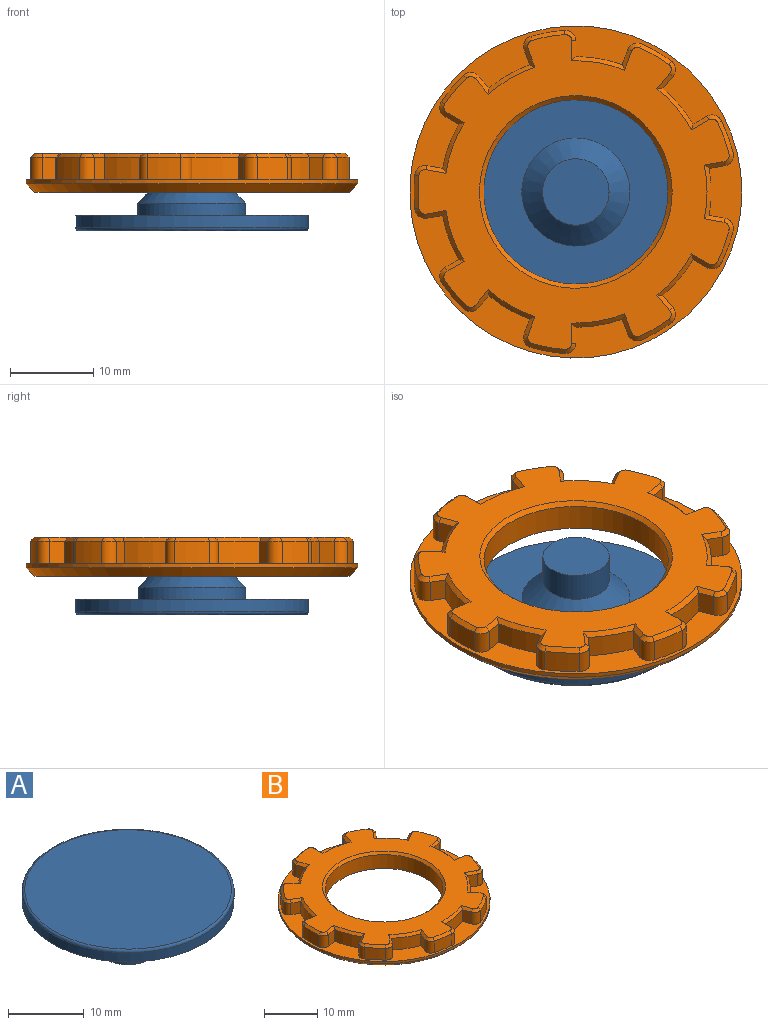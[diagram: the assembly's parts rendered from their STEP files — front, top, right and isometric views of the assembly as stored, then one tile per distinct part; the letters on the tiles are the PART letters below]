
ASSEMBLY  parts=2 mates=1
PART A: 8 faces, bbox 30.3x30.3x9.4 mm
  f0: plane 27.3x27.3mm, normal (0,0,1), area 585.3mm2, adj f7
  f1: plane 8x8mm, normal (0,0,-1), area 50.3mm2, adj f2
  f2: cylinder r=4mm len=8mm, axis (0,0,1), area 88mm2, adj f1,f3
  f3: cone r=4mm half-angle=45deg, axis (0,0,1), area 116.6mm2, adj f2,f4
  f4: cylinder r=6.5mm len=13mm, axis (0,0,1), area 61.3mm2, adj f3,f5
  f5: plane 28x28mm, normal (0,0,-1), area 483mm2, adj f4,f6
  f6: cylinder r=14mm len=28mm, axis (0,0,1), area 131.9mm2, adj f5,f7
  f7: torus R=13.65mm, axis (0,0,1), area 47.9mm2, adj f0,f6
PART B: 117 faces, bbox 40x40x4.7 mm
  f0: cylinder r=11.1mm len=22.2mm, axis (0,0,-1), area 223.2mm2, adj f110,f115
  f1: cylinder r=16.3mm len=5.32mm, axis (0,0,-1), area 15.4mm2, adj f2,f53,f97,f113
  f2: plane 2.7x1.88mm, normal (0.17,0.98,0), area 5.1mm2, adj f1,f7,f95,f113
  f3: cylinder r=19.5mm len=4.13mm, axis (0,0,-1), area 11.2mm2, adj f7,f8,f91,f113
  f4: plane 2.7x1.88mm, normal (0.17,-0.98,0), area 5.1mm2, adj f5,f8,f87,f113
  f5: cylinder r=16.3mm len=5.32mm, axis (0,0,-1), area 15.4mm2, adj f4,f9,f85,f113
  f6: plane 37.91x37.46mm, normal (0,0,1), area 505.2mm2, adj f56,f57,f58,f59,f60,f61,f62,f63
  f7: cylinder r=1.25mm len=2.7mm, axis (0,0,-1), area 5.5mm2, adj f2,f3,f93,f113
  f8: cylinder r=1.25mm len=2.7mm, axis (0,0,-1), area 5.5mm2, adj f3,f4,f89,f113
  f9: plane 2.7x1.65mm, normal (-0.5,0.87,0), area 5.1mm2, adj f5,f13,f83,f113
  f10: cylinder r=19.5mm len=3.16mm, axis (0,0,-1), area 11.2mm2, adj f13,f14,f79,f113
  f11: plane 2.7x1.46mm, normal (0.77,-0.64,0), area 5.1mm2, adj f12,f14,f75,f113
  f12: cylinder r=16.3mm len=4.9mm, axis (0,0,-1), area 15.4mm2, adj f11,f15,f73,f113
  f13: cylinder r=1.25mm len=2.7mm, axis (0,0,-1), area 5.5mm2, adj f9,f10,f81,f113
  f14: cylinder r=1.25mm len=2.7mm, axis (0,0,-1), area 5.5mm2, adj f10,f11,f77,f113
  f15: plane 2.7x1.79mm, normal (-0.94,0.34,0), area 5.1mm2, adj f12,f19,f71,f113
  f16: cylinder r=19.5mm len=4.06mm, axis (0,0,-1), area 11.2mm2, adj f19,f20,f67,f113
  f17: plane 2.7x1.91mm, normal (1,0,0), area 5.1mm2, adj f18,f20,f63,f113
  f18: cylinder r=16.3mm len=5.58mm, axis (0,0,-1), area 15.4mm2, adj f17,f21,f61,f113
  f19: cylinder r=1.25mm len=2.7mm, axis (0,0,-1), area 5.5mm2, adj f15,f16,f69,f113
  f20: cylinder r=1.25mm len=2.7mm, axis (0,0,-1), area 5.5mm2, adj f16,f17,f65,f113
  f21: plane 2.7x1.79mm, normal (-0.94,-0.34,0), area 5.1mm2, adj f18,f25,f59,f113
  f22: cylinder r=19.5mm len=3.57mm, axis (0,0,-1), area 11.2mm2, adj f25,f26,f56,f113
  f23: plane 2.7x1.46mm, normal (0.77,0.64,0), area 5.1mm2, adj f24,f26,f60,f113
  f24: cylinder r=16.3mm len=4.34mm, axis (0,0,-1), area 15.4mm2, adj f23,f27,f62,f113
  f25: cylinder r=1.25mm len=2.7mm, axis (0,0,-1), area 5.5mm2, adj f21,f22,f57,f113
  f26: cylinder r=1.25mm len=2.7mm, axis (0,0,-1), area 5.5mm2, adj f22,f23,f58,f113
  f27: plane 2.7x1.65mm, normal (-0.5,-0.87,0), area 5.1mm2, adj f24,f31,f64,f113
  f28: cylinder r=19.5mm len=3.88mm, axis (0,0,-1), area 11.2mm2, adj f31,f32,f68,f113
  f29: plane 2.7x1.88mm, normal (0.17,0.98,0), area 5.1mm2, adj f30,f32,f72,f113
  f30: cylinder r=16.3mm len=5.66mm, axis (0,0,-1), area 15.4mm2, adj f29,f33,f74,f113
  f31: cylinder r=1.25mm len=2.7mm, axis (0,0,-1), area 5.5mm2, adj f27,f28,f66,f113
  f32: cylinder r=1.25mm len=2.7mm, axis (0,0,-1), area 5.5mm2, adj f28,f29,f70,f113
  f33: plane 2.7x1.88mm, normal (0.17,-0.98,0), area 5.1mm2, adj f30,f37,f76,f113
  f34: cylinder r=19.5mm len=3.88mm, axis (0,0,-1), area 11.2mm2, adj f37,f38,f80,f113
  f35: plane 2.7x1.65mm, normal (-0.5,0.87,0), area 5.1mm2, adj f36,f38,f84,f113
  f36: cylinder r=16.3mm len=4.34mm, axis (0,0,-1), area 15.4mm2, adj f35,f39,f86,f113
  f37: cylinder r=1.25mm len=2.7mm, axis (0,0,-1), area 5.5mm2, adj f33,f34,f78,f113
  f38: cylinder r=1.25mm len=2.7mm, axis (0,0,-1), area 5.5mm2, adj f34,f35,f82,f113
  f39: plane 2.7x1.46mm, normal (0.77,-0.64,0), area 5.1mm2, adj f36,f43,f88,f113
  f40: cylinder r=19.5mm len=3.57mm, axis (0,0,-1), area 11.2mm2, adj f43,f44,f92,f113
  f41: plane 2.7x1.79mm, normal (-0.94,0.34,0), area 5.1mm2, adj f42,f44,f96,f113
  f42: cylinder r=16.3mm len=5.58mm, axis (0,0,-1), area 15.4mm2, adj f41,f45,f98,f113
  f43: cylinder r=1.25mm len=2.7mm, axis (0,0,-1), area 5.5mm2, adj f39,f40,f90,f113
  f44: cylinder r=1.25mm len=2.7mm, axis (0,0,-1), area 5.5mm2, adj f40,f41,f94,f113
  f45: plane 2.7x1.91mm, normal (1,0,0), area 5.1mm2, adj f42,f49,f100,f113
  f46: cylinder r=19.5mm len=4.06mm, axis (0,0,-1), area 11.2mm2, adj f49,f50,f104,f113
  f47: plane 2.7x1.79mm, normal (-0.94,-0.34,0), area 5.1mm2, adj f48,f50,f108,f113
  f48: cylinder r=16.3mm len=4.9mm, axis (0,0,-1), area 15.4mm2, adj f47,f51,f109,f113
  f49: cylinder r=1.25mm len=2.7mm, axis (0,0,-1), area 5.5mm2, adj f45,f46,f102,f113
  f50: cylinder r=1.25mm len=2.7mm, axis (0,0,-1), area 5.5mm2, adj f46,f47,f106,f113
  f51: plane 2.7x1.46mm, normal (0.77,0.64,0), area 5.1mm2, adj f48,f54,f107,f113
  f52: cylinder r=19.5mm len=3.16mm, axis (0,0,-1), area 11.2mm2, adj f54,f55,f103,f113
  f53: plane 2.7x1.65mm, normal (-0.5,-0.87,0), area 5.1mm2, adj f1,f55,f99,f113
  f54: cylinder r=1.25mm len=2.7mm, axis (0,0,-1), area 5.5mm2, adj f51,f52,f105,f113
  f55: cylinder r=1.25mm len=2.7mm, axis (0,0,-1), area 5.5mm2, adj f52,f53,f101,f113
  f56: cone r=19.5mm half-angle=45deg, axis (0,0,-1), area 2.9mm2, adj f6,f22,f57,f58
  f57: cone r=0.75mm half-angle=45deg, axis (0,0,-1), area 1.2mm2, adj f6,f25,f56,f59
  f58: cone r=0.75mm half-angle=45deg, axis (0,0,-1), area 1.2mm2, adj f6,f26,f56,f60
  f59: plane 2.45x1.13mm, normal (-0.66,-0.24,0.71), area 1.5mm2, adj f6,f21,f57,f61
  f60: plane 1.94x1.86mm, normal (0.54,0.45,0.71), area 1.5mm2, adj f6,f23,f58,f62
  f61: cone r=16.3mm half-angle=45deg, axis (0,0,-1), area 4.3mm2, adj f6,f18,f59,f63
  f62: cone r=16.3mm half-angle=45deg, axis (0,0,-1), area 4.3mm2, adj f6,f24,f60,f64
  f63: plane 2.42x0.51mm, normal (0.71,0,0.71), area 1.5mm2, adj f6,f17,f61,f65
  f64: plane 2.1x1.65mm, normal (-0.35,-0.61,0.71), area 1.5mm2, adj f6,f27,f62,f66
  f65: cone r=0.75mm half-angle=45deg, axis (0,0,-1), area 1.2mm2, adj f6,f20,f63,f67
  f66: cone r=0.75mm half-angle=45deg, axis (0,0,-1), area 1.2mm2, adj f6,f31,f64,f68
  f67: cone r=19.5mm half-angle=45deg, axis (0,0,-1), area 2.9mm2, adj f6,f16,f65,f69
  f68: cone r=19.5mm half-angle=45deg, axis (0,0,-1), area 2.9mm2, adj f6,f28,f66,f70
  f69: cone r=0.75mm half-angle=45deg, axis (0,0,-1), area 1.2mm2, adj f6,f19,f67,f71
  f70: cone r=0.75mm half-angle=45deg, axis (0,0,-1), area 1.2mm2, adj f6,f32,f68,f72
  f71: plane 2.28x1.3mm, normal (-0.66,0.24,0.71), area 1.5mm2, adj f6,f15,f69,f73
  f72: plane 2.47x0.83mm, normal (0.12,0.7,0.71), area 1.5mm2, adj f6,f29,f70,f74
  f73: cone r=16.3mm half-angle=45deg, axis (0,0,-1), area 4.3mm2, adj f6,f12,f71,f75
  f74: cone r=16.3mm half-angle=45deg, axis (0,0,-1), area 4.3mm2, adj f6,f30,f72,f76
  f75: plane 2.18x1.62mm, normal (0.54,-0.45,0.71), area 1.5mm2, adj f6,f11,f73,f77
  f76: plane 2.47x0.83mm, normal (0.12,-0.7,0.71), area 1.5mm2, adj f6,f33,f74,f78
  f77: cone r=0.75mm half-angle=45deg, axis (0,0,-1), area 1.2mm2, adj f6,f14,f75,f79
  f78: cone r=0.75mm half-angle=45deg, axis (0,0,-1), area 1.2mm2, adj f6,f37,f76,f80
  f79: cone r=19.5mm half-angle=45deg, axis (0,0,-1), area 2.9mm2, adj f6,f10,f77,f81
  f80: cone r=19.5mm half-angle=45deg, axis (0,0,-1), area 2.9mm2, adj f6,f34,f78,f82
  f81: cone r=0.75mm half-angle=45deg, axis (0,0,-1), area 1.2mm2, adj f6,f13,f79,f83
  f82: cone r=0.75mm half-angle=45deg, axis (0,0,-1), area 1.2mm2, adj f6,f38,f80,f84
  f83: plane 2.35x1.39mm, normal (-0.35,0.61,0.71), area 1.5mm2, adj f6,f9,f81,f85
  f84: plane 2.1x1.65mm, normal (-0.35,0.61,0.71), area 1.5mm2, adj f6,f35,f82,f86
  f85: cone r=16.3mm half-angle=45deg, axis (0,0,-1), area 4.3mm2, adj f5,f6,f83,f87
  f86: cone r=16.3mm half-angle=45deg, axis (0,0,-1), area 4.3mm2, adj f6,f36,f84,f88
  f87: plane 2.39x0.92mm, normal (0.12,-0.7,0.71), area 1.5mm2, adj f4,f6,f85,f89
  f88: plane 1.94x1.86mm, normal (0.54,-0.45,0.71), area 1.5mm2, adj f6,f39,f86,f90
  f89: cone r=0.75mm half-angle=45deg, axis (0,0,-1), area 1.2mm2, adj f6,f8,f87,f91
  f90: cone r=0.75mm half-angle=45deg, axis (0,0,-1), area 1.2mm2, adj f6,f43,f88,f92
  f91: cone r=19.5mm half-angle=45deg, axis (0,0,-1), area 2.9mm2, adj f3,f6,f89,f93
  f92: cone r=19.5mm half-angle=45deg, axis (0,0,-1), area 2.9mm2, adj f6,f40,f90,f94
  f93: cone r=0.75mm half-angle=45deg, axis (0,0,-1), area 1.2mm2, adj f6,f7,f91,f95
  f94: cone r=0.75mm half-angle=45deg, axis (0,0,-1), area 1.2mm2, adj f6,f44,f92,f96
  f95: plane 2.39x0.92mm, normal (0.12,0.7,0.71), area 1.5mm2, adj f2,f6,f93,f97
  f96: plane 2.45x1.13mm, normal (-0.66,0.24,0.71), area 1.5mm2, adj f6,f41,f94,f98
  f97: cone r=15.8mm half-angle=45deg, axis (0,0,-1), area 4.3mm2, adj f1,f6,f95,f99
  f98: cone r=16.3mm half-angle=45deg, axis (0,0,-1), area 4.3mm2, adj f6,f42,f96,f100
  f99: plane 2.35x1.39mm, normal (-0.35,-0.61,0.71), area 1.5mm2, adj f6,f53,f97,f101
  f100: plane 2.42x0.51mm, normal (0.71,0,0.71), area 1.5mm2, adj f6,f45,f98,f102
  f101: cone r=0.75mm half-angle=45deg, axis (0,0,-1), area 1.2mm2, adj f6,f55,f99,f103
  f102: cone r=0.75mm half-angle=45deg, axis (0,0,-1), area 1.2mm2, adj f6,f49,f100,f104
  f103: cone r=19.5mm half-angle=45deg, axis (0,0,-1), area 2.9mm2, adj f6,f52,f101,f105
  f104: cone r=19.5mm half-angle=45deg, axis (0,0,-1), area 2.9mm2, adj f6,f46,f102,f106
  f105: cone r=0.75mm half-angle=45deg, axis (0,0,-1), area 1.2mm2, adj f6,f54,f103,f107
  f106: cone r=0.75mm half-angle=45deg, axis (0,0,-1), area 1.2mm2, adj f6,f50,f104,f108
  f107: plane 2.18x1.62mm, normal (0.54,0.45,0.71), area 1.5mm2, adj f6,f51,f105,f109
  f108: plane 2.28x1.3mm, normal (-0.66,-0.24,0.71), area 1.5mm2, adj f6,f47,f106,f109
  f109: cone r=16.3mm half-angle=45deg, axis (0,0,-1), area 4.3mm2, adj f6,f48,f107,f108
  f110: cone r=11.1mm half-angle=45deg, axis (0,0,1), area 50.4mm2, adj f0,f6
  f111: cylinder r=20mm len=40mm, axis (0,0,1), area 62.8mm2, adj f113,f114
  f112: plane 38x38mm, normal (0,0,-1), area 116.2mm2, adj f114,f116
  f113: plane 40x40mm, normal (0,0,1), area 248.7mm2, adj f1,f2,f3,f4,f5,f7,f8,f9
  f114: cone r=20mm half-angle=45deg, axis (0,0,1), area 173.3mm2, adj f111,f112
  f115: plane 34x34mm, normal (0,0,-1), area 520.8mm2, adj f0,f116
  f116: cone r=17mm half-angle=45deg, axis (0,0,-1), area 155.5mm2, adj f112,f115
PLACE A rot(axis=(1,0,0),180deg) t=(-16.82,-2.04,-1.81)mm
PLACE B rot(axis=(-0.94,0,-0.33),0deg) t=(-16.82,-2.04,-2.01)mm
MATE fastened B.f116 <-> A.f3  axis (0,0,1) through (-16.82,-2.04,1.19)mm
